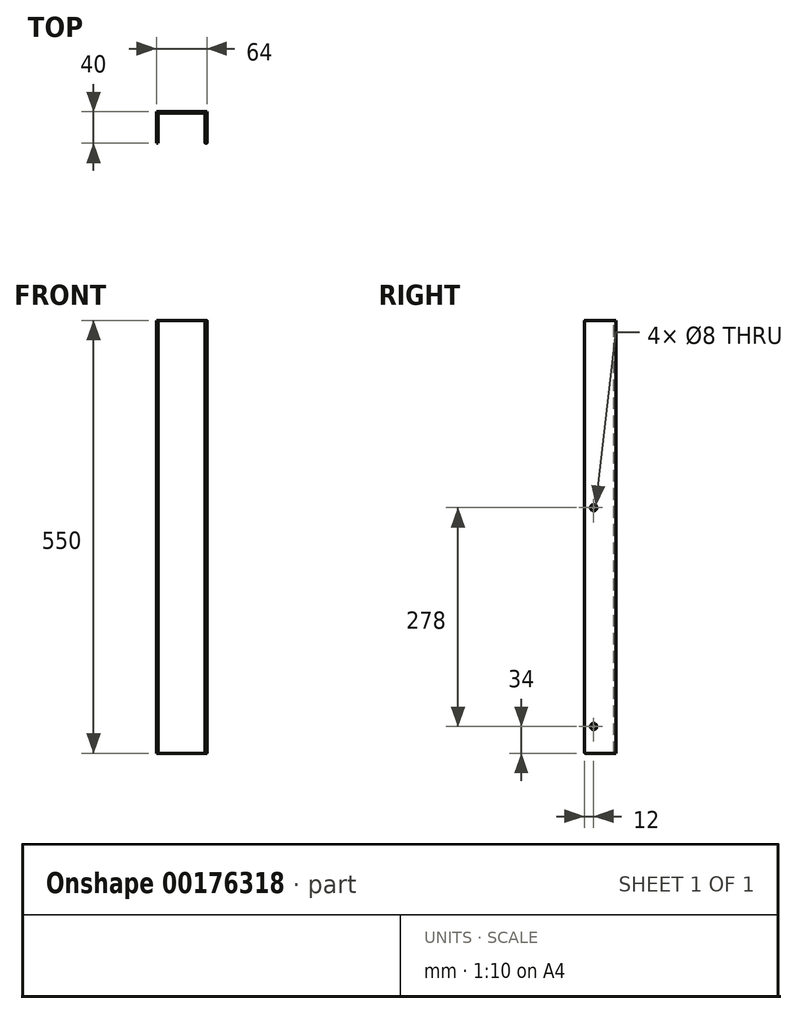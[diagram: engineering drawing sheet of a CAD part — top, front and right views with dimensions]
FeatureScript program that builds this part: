
annotation { "Feature Type Name" : "Feature", "Feature Type Description" : "" }
export const myFeature = defineFeature(function(context is Context, id is Id, definition is map)
    precondition{}
    {
        {
            var Q0;
            Q0=qCreatedBy(makeId("Front.planeOp"),FACE);
            var sketch = newSketch(context, id + "F0", { "sketchPlane" : qUnion([Q0])});
            skLineSegment(sketch, "E0", {"start": v(0, 0) * mm, "end": v(0, 550) * mm});
            skLineSegment(sketch, "E1", {"start": v(0, 550) * mm, "end": v(-60, 550) * mm});
            skLineSegment(sketch, "E2", {"start": v(-60, 550) * mm, "end": v(-60, 0) * mm});
            skLineSegment(sketch, "E3", {"start": v(-60, 0) * mm, "end": v(0, 0) * mm});
            skSolve(sketch);
        }
        {
            var Q0;
            Q0 = qSketchRegion(id + "F0", true);
            extrude(context, id + "F1", {"entities" : qUnion([Q0]), "oppositeDirection" : true, "depth" : 2 * mm});
        }
        {
            var Q0;
            Q0=makeQuery(id+"F1.opExtrude","SWEPT_FACE",FACE,{"disambiguationData":[OSD([sQuery(id+"F0.wireOp",EDGE,"E0")])]});
            var sketch = newSketch(context, id + "F2", { "sketchPlane" : qUnion([Q0])});
            skLineSegment(sketch, "E4", {"start": v(2, 550) * mm, "end": v(-38, 550) * mm});
            skPoint(sketch, "E4.endSnap0", {"position": v(1, 550) * mm});
            skLineSegment(sketch, "E5", {"start": v(-38, 550) * mm, "end": v(-38, 0) * mm});
            skLineSegment(sketch, "E6", {"start": v(-38, 0) * mm, "end": v(0, 0) * mm});
            skSolve(sketch);
        }
        {
            var Q0;
            {var subQ2=sQuery(id+"F2.wireOp",EDGE,"E5");Q0=makeQuery(id+"F2.imprint","IMPRINT",FACE,{"disambiguationData":[TD([[makeQuery(id+"F2.imprint","IMPRINT",EDGE,{"derivedFrom":subQ2}),1.0]])]});}
            var Q1;
            {var subQ1=sQuery(id+"F0.wireOp",EDGE,"E0");var subQ2=makeQuery(id+"F1.opExtrude","CAP_EDGE",EDGE,{"disambiguationData":[OSD([subQ1])],"isStart":true});Q1=makeQuery(id+"F2.imprint","IMPRINT",FACE,{"disambiguationData":[TD([[makeQuery(id+"F2.imprint","IMPRINT",EDGE,{"derivedFrom":subQ2}),-1.0]])]});}
            extrude(context, id + "F3", {"entities" : qUnion([Q0, Q1]), "operationType" : NewBodyOperationType.ADD, "depth" : 2 * mm});
        }
        {
            var Q0;
            Q0=makeQuery(id+"F1.opExtrude","SWEPT_FACE",FACE,{"disambiguationData":[OSD([sQuery(id+"F0.wireOp",EDGE,"E2")])]});
            var sketch = newSketch(context, id + "F4", { "sketchPlane" : qUnion([Q0])});
            skLineSegment(sketch, "E7", {"start": v(-2, 550) * mm, "end": v(38, 550) * mm});
            skLineSegment(sketch, "E8", {"start": v(38, 550) * mm, "end": v(38, 0) * mm});
            skLineSegment(sketch, "E9", {"start": v(38, 0) * mm, "end": v(-2, 0) * mm});
            skSolve(sketch);
        }
        {
            var Q0;
            {var subQ2=sQuery(id+"F4.wireOp",EDGE,"E8");Q0=makeQuery(id+"F4.imprint","IMPRINT",FACE,{"disambiguationData":[TD([[makeQuery(id+"F4.imprint","IMPRINT",EDGE,{"derivedFrom":subQ2}),-1.0]])]});}
            var Q1;
            {var subQ1=sQuery(id+"F0.wireOp",EDGE,"E2");var subQ2=makeQuery(id+"F1.opExtrude","CAP_EDGE",EDGE,{"disambiguationData":[OSD([subQ1])],"isStart":true});Q1=makeQuery(id+"F4.imprint","IMPRINT",FACE,{"disambiguationData":[TD([[makeQuery(id+"F4.imprint","IMPRINT",EDGE,{"derivedFrom":subQ2}),-1.0]])]});}
            extrude(context, id + "F5", {"entities" : qUnion([Q0, Q1]), "operationType" : NewBodyOperationType.ADD, "depth" : 2 * mm});
        }
        {
            var Q0;
            Q0=makeQuery(id+"F5.opExtrude","SWEPT_EDGE",EDGE,{"disambiguationData":[OSD([sQuery(id+"F4.wireOp",EDGE,"E8"),sQuery(id+"F4.wireOp",EDGE,"E9")])]});
            var Q1;
            Q1=makeQuery(id+"F3.opExtrude","SWEPT_EDGE",EDGE,{"disambiguationData":[OSD([sQuery(id+"F2.wireOp",EDGE,"E5"),sQuery(id+"F2.wireOp",EDGE,"E6")])]});
            fillet(context, id + "F6", {"entities" : qUnion([Q0, Q1]), "radius" : 1.5 * mm, "tangentPropagation" : true, "allowEdgeOverflow" : false});
        }
        {
            var Q0;
            Q0=makeQuery(id+"F5.opExtrude","SWEPT_EDGE",EDGE,{"disambiguationData":[OSD([sQuery(id+"F4.wireOp",EDGE,"E7"),sQuery(id+"F4.wireOp",EDGE,"E8")])]});
            var Q1;
            Q1=makeQuery(id+"F3.opExtrude","SWEPT_EDGE",EDGE,{"disambiguationData":[OSD([sQuery(id+"F2.wireOp",EDGE,"E4"),sQuery(id+"F2.wireOp",EDGE,"E5")])]});
            fillet(context, id + "F7", {"entities" : qUnion([Q0, Q1]), "radius" : 1.5 * mm, "tangentPropagation" : true, "allowEdgeOverflow" : false});
        }
        {
            var Q0;
            Q0=makeQuery(id+"F5.opExtrude","CAP_FACE",FACE,{"disambiguationData":[OSD([sQuery(id+"F0.wireOp",EDGE,"E2"),sQuery(id+"F4.wireOp",EDGE,"E7"),sQuery(id+"F4.wireOp",EDGE,"E8"),sQuery(id+"F4.wireOp",EDGE,"E9")])],"isStart":false});
            var sketch = newSketch(context, id + "F8", { "sketchPlane" : qUnion([Q0])});
            skCircle(sketch, "E10", {"center": v(26, 312) * mm, "radius": 4 * mm});
            skCircle(sketch, "E11", {"center": v(26, 34) * mm, "radius": 4 * mm});
            skSolve(sketch);
        }
        {
            var Q0;
            Q0=makeQuery(id+"F8.imprint","IMPRINT",FACE,{"disambiguationData":[TD([[makeQuery(id+"F8.imprint","IMPRINT",EDGE,{"derivedFrom":sQuery(id+"F8.wireOp",EDGE,"E10")}),1.0]])]});
            var Q1;
            Q1=makeQuery(id+"F8.imprint","IMPRINT",FACE,{"disambiguationData":[TD([[makeQuery(id+"F8.imprint","IMPRINT",EDGE,{"derivedFrom":sQuery(id+"F8.wireOp",EDGE,"E11")}),1.0]])]});
            extrude(context, id + "F9", {"entities" : qUnion([Q0, Q1]), "operationType" : NewBodyOperationType.REMOVE, "endBound" : BoundingType.THROUGH_ALL, "oppositeDirection" : true, "depth" : 25 * mm});
        }
    });
